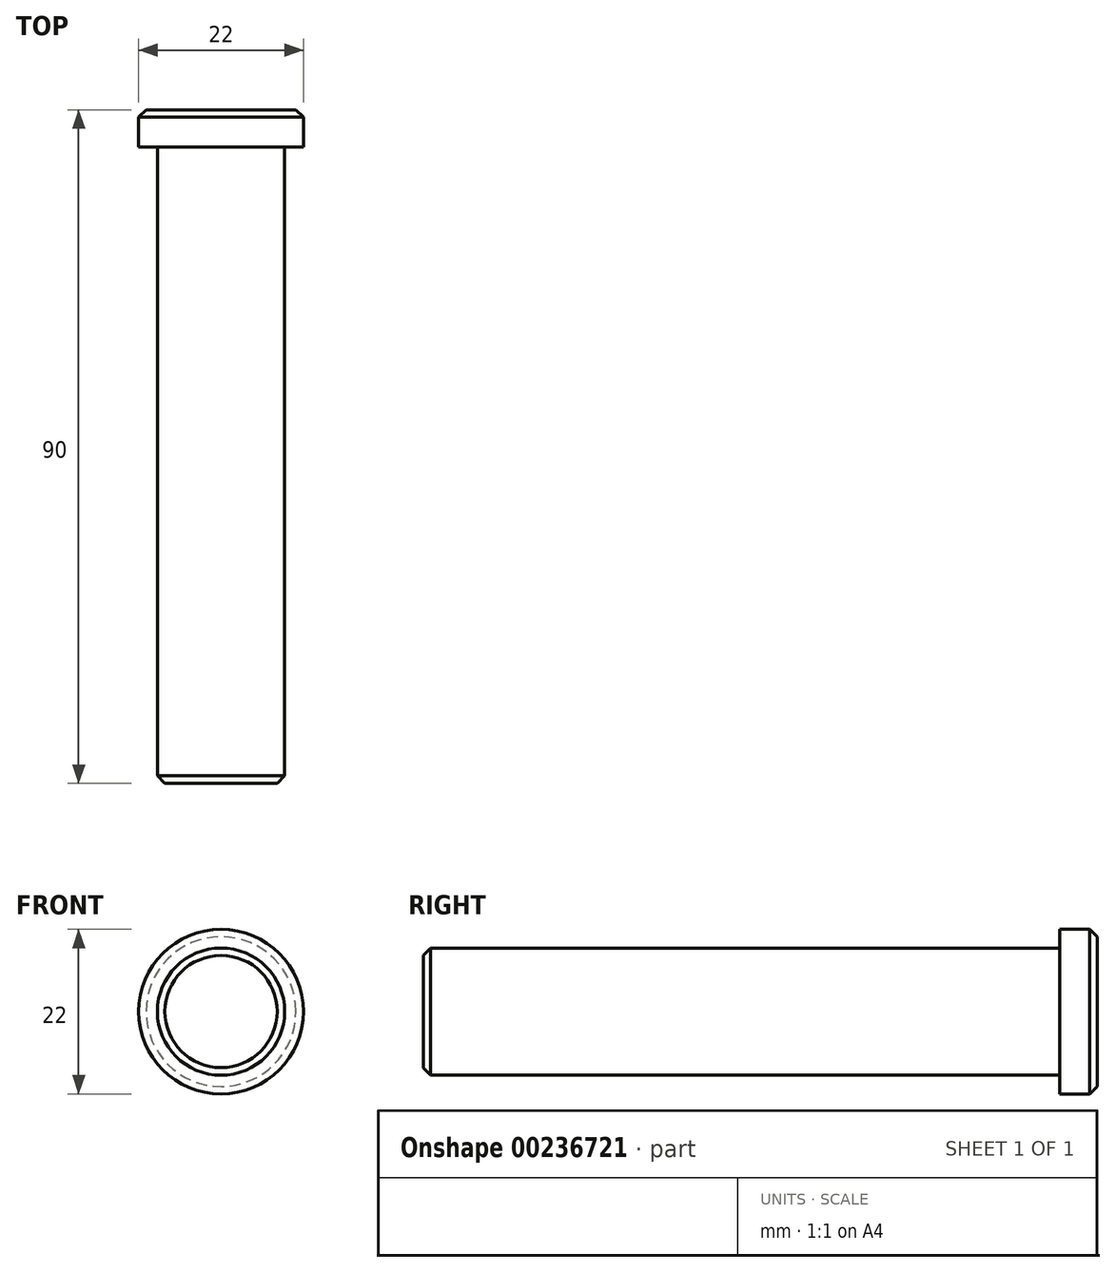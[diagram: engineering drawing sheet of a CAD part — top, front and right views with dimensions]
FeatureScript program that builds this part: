
annotation { "Feature Type Name" : "Feature", "Feature Type Description" : "" }
export const myFeature = defineFeature(function(context is Context, id is Id, definition is map)
    precondition{}
    {
        {
            var Q0;
            Q0=qCreatedBy(makeId("Front.planeOp"),FACE);
            var sketch = newSketch(context, id + "F0", { "sketchPlane" : qUnion([Q0])});
            skCircle(sketch, "E0", {"center": v(0, 0) * mm, "radius": 11 * mm});
            skSolve(sketch);
        }
        {
            var Q0;
            Q0=qSketchRegion(id+"F0",true);
            extrude(context, id + "F1", {"entities" : qUnion([Q0]), "offsetDistance" : 25 * mm, "depth" : 5 * mm});
        }
        {
            var Q0;
            Q0=makeQuery(id+"F1.opExtrude","CAP_FACE",FACE,{"disambiguationData":[OSD([sQuery(id+"F0.wireOp",EDGE,"E0")])],"isStart":false});
            var sketch = newSketch(context, id + "F2", { "sketchPlane" : qUnion([Q0])});
            skCircle(sketch, "E1", {"center": v(0, 0) * mm, "radius": 8.5 * mm});
            skSolve(sketch);
        }
        {
            var Q0;
            Q0=qSketchRegion(id+"F2",true);
            extrude(context, id + "F3", {"entities" : qUnion([Q0]), "operationType" : NewBodyOperationType.ADD, "depth" : 85 * mm});
        }
        {
            var Q0;
            Q0=makeQuery(id+"F1.opExtrude","CAP_EDGE",EDGE,{"disambiguationData":[OSD([sQuery(id+"F0.wireOp",EDGE,"E0")])],"isStart":true});
            chamfer(context, id + "F4", {"entities" : qUnion([Q0]), "width" : 1 * mm, "tangentPropagation" : true});
        }
        {
            var Q0;
            Q0=makeQuery(id+"F3.opExtrude","CAP_EDGE",EDGE,{"disambiguationData":[OSD([sQuery(id+"F2.wireOp",EDGE,"E1")])],"isStart":false});
            chamfer(context, id + "F5", {"entities" : qUnion([Q0]), "width" : 1 * mm, "tangentPropagation" : true});
        }
    });
